# Revit family: Sanitary_Showers_hansgrohe_26925USA-Raindance-E-Overhead-shower-400_9988
name_source: partatom
category: Plumbing Fixtures
revit_build: Autodesk Revit 2018 (Build: 20170223_1515(x64)
units: mm (PartAtom-declared; Revit-internal decimal feet)

## family parameters
Always vertical = No
Cut with Voids When Loaded = No
OmniClass Number = 23.45.05.14.17
OmniClass Title = Showers
Part Type = Normal
Room Calculation Point = No
Round Connector Dimension = Use Diameter
Shared = No
Work Plane-Based = Yes

## types (1)
- 001 Chrome
    BIMobject category = Showers
    Default Elevation = 1219.2 mm  [stored 4 ft]
    Description = Raindance E Overhead shower 400/400 1jet 2.5 GPM
    Design country = Germany
    EAN code = 4059625339336
    Edition number = 1
    GTIN code = https://4059625339336
    IFC Classification = Sanitary Terminal
    Installation instructions = https://www.hansgrohe.com
    Manufacturer = Hansgrohe
    Manufacturer country = Germany
    Manufacturer name = hansgrohe
    Material 1 = Hansgrohe - Metal - 001 Chrome
    Material main = Chrome
    Model = 26925USA
    OmniClass Code = 23-31 17 00
    OmniClass Description = Showers
    Product Guid = f59e7997-5065-47f6-a7a9-17dd7438a6da
    Product SKU = 26925USA
    Product data url = https://bimobject.com
    Product family = Raindance E
    Product group = Overhead showers
    Product name = 26925USA Raindance E Overhead shower 400/400 1jet 2.5 GPM
    Product url = https://www.hansgrohe.com
    QR code = https://bimobject.com
    URL = https://www.hansgrohe.com
    Water  Inlet = 13 mm
    Water Inlet Description = Water  Inlet 12.7mm
    Weight Net (Kg) = 5.1

note: [stored X ft] marks values corroborated as IEEE doubles in the binary element streams (Revit-internal decimal feet)

## geometry (parser evidence)
native form markers: Sweep x2
no freeform markers — native parametric forms only
